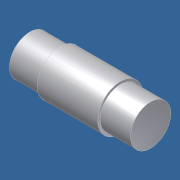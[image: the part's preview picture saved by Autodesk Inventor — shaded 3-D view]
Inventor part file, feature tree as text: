
AUTODESK INVENTOR PART (.ipt)
format: ipt  version: unknown  size: 174,080 bytes
history: native  units: in
note: dims shown in document units (in); Inventor stores cm internally (conversion verified against a paired STEP export)
features: revolve x1, sketch x1
ambient origin geometry x8: Origin, YZ Plane, XZ Plane, XY Plane, X Axis, Y Axis, Z Axis, Center Point
bodies: Solid1 (feature_tree)
feature tree (2):
  revolve  "Revolution1"  [1 undecoded]
  sketch  "Sketch1"  dims[d0=0.1875in d1=0.1875in d2=0.75in d3=0.125in d4=0.125in d5=0.1406in d6=90.0deg]
note: 1 required parameter value undecoded (feature->parameter linkage not recoverable at this tier; creation-order binding heuristic only, values carry confidence <= 0.55)
